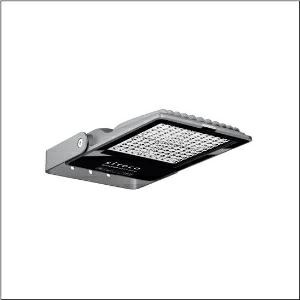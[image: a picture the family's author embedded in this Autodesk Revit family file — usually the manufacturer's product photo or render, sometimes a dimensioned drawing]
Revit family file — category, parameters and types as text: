
# Revit family: sicompact_r__31_mini___pl32_5xa7571b2k23_8fae
name_source: partatom
category: Lighting Fixtures
units: mm (PartAtom-declared; Revit-internal decimal feet)

## family parameters
Cut with Voids When Loaded = No
Host = Face
Light Source = No
Part Type = Normal
Room Calculation Point = No
Round Connector Dimension = Use Diameter
Shared = No

## types (1)
- SiCompact® 31 mini  PL32 (1 x LED, 8000 lm, 47 W, 4000K)
    Apparent Load = 47 VA
    CIE Flux Codes = 32 69 98 100 100
    Color Rendering = 70
    Color Temperature = 4000K
    Default Elevation = 1800 mm
    Description = SiCompact® 31 mini, floodlight, primary light control with lens, of plastic, of toughened safety glass, transparent, light distribution: PL32, light emission: direct distribution, primary light characteristic: asymmetric, installation type: surface-mounted, LED, High Power LED, rated luminous flux: 8.000lm, luminous efficacy: 170lm/W, light colour: 740, colour temperature: 4000K, control gear: ECG, with cable, 3x 1.5mm², mains connection: 220..240V, AC, 50/60Hz, connection cable pre-assembled, cable length: 2m, rated input power: 47W, of diecast aluminium, specular, metallic grey (RAL 9006), length: 461mm, width: 261mm, height: 62mm, bracket, of sheet steel, coated, metallic grey (RAL 9006), ON/OFF, protection rating (complete): IP66, insulation class (complete): insulation class I (protective earthing), certification: CE, ENEC, impact resistance: IK08, permissible operating ambient temperature: -40..+45°C, packaging unit: 1 piece

Light Distribution: PL32
    Height = 62 mm  [stored 0.203412 ft]
    Lamp = 1 x LED
    Lamp Light Flux = 8000 lm
    Lamp Power = 47 W
    Lamp count = 1
    Length = 460 mm
    Luminous efficacy = 170 lm/W
    Manufacturer = Siteco
    ModVariant = No
    Model = 5XA7571B2K23
    Mounting Place = Wall
    Mounting Type = Surface mounted
    Number of Poles = 1
    OnlyDefault = Yes
    Power Factor = 1
    Product Name = SiCompact® 31 mini | PL32
    Product group = floodlight | wall mounted
    ProductGroupID = 2001
    Protection Class = Protection class I
    Protection Degree = IP 66
    RLX_Detail_Level = 1
    RLX_Emergency_Light_Flux = 0 lm
    RLX_Emergency_Type = 0
    RLX_Emergency_Type_DB = No
    RlxData = <blob elided: 126773 chars, md5=e86a1a1d>
    Socket = socket
    Standby Power = 0 W
    System Light Flux = 8000 lm
    System Power = 47 W
    Type Comments = Product without accessories
    Type Image = l_1006951.jpg
    URL = http://relux.com
    VarID = ---
    Voltage = 0 V
    Weight = 0.00 kg
    Width = 260 mm

note: [stored X ft] marks values corroborated as IEEE doubles in the binary element streams (Revit-internal decimal feet)

## geometry (parser evidence)
native form markers: Blend x4, Sweep x11
no freeform markers — native parametric forms only
